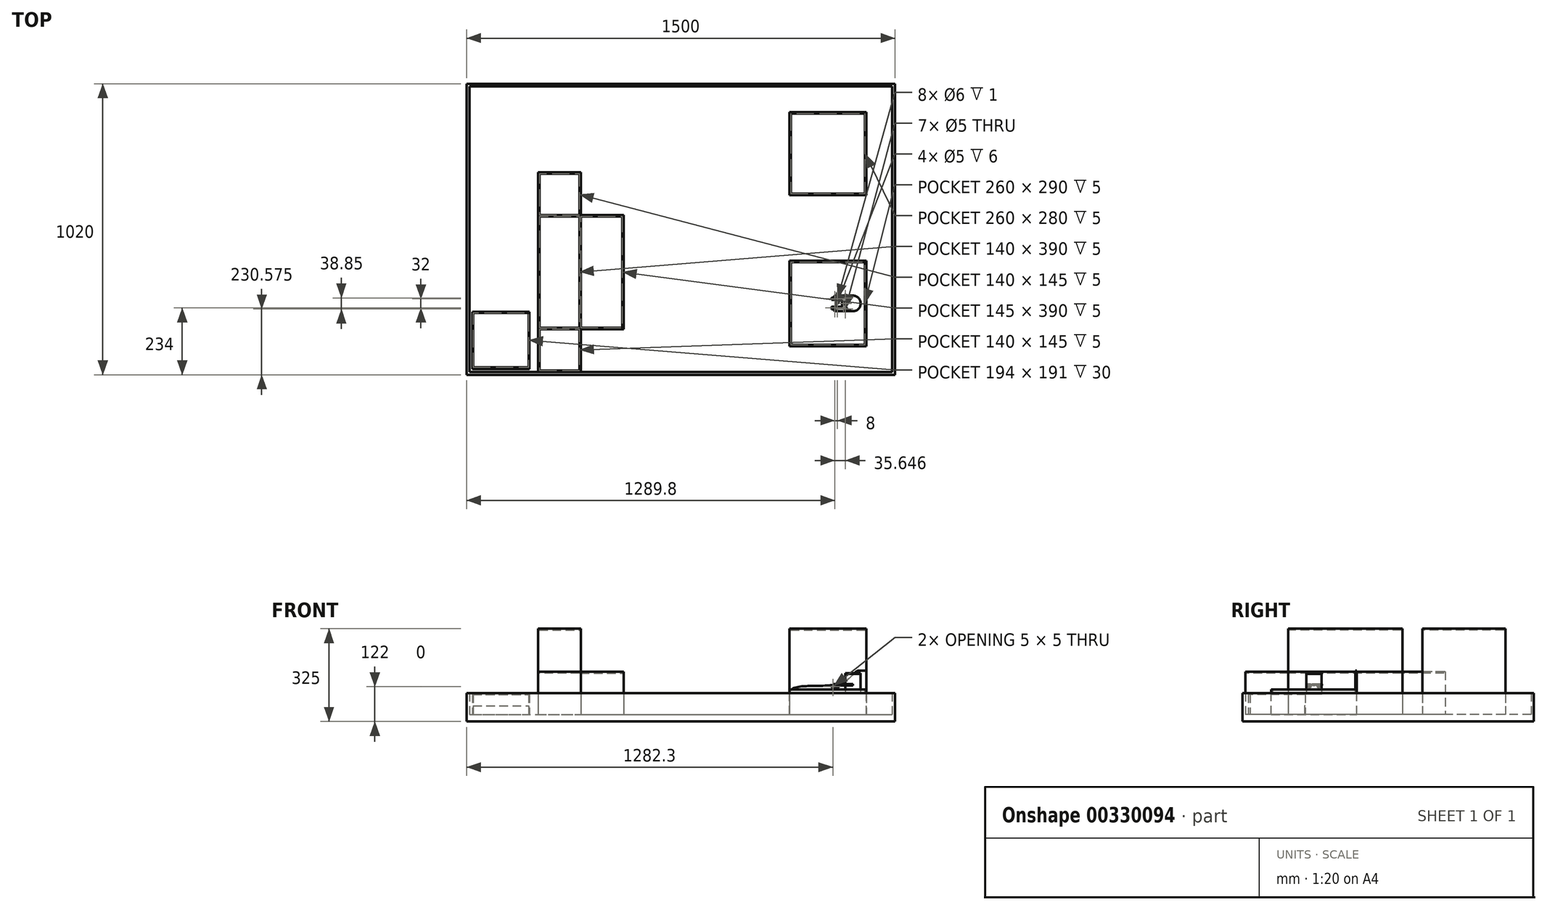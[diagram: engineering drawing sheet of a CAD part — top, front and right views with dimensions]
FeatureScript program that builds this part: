
annotation { "Feature Type Name" : "Feature", "Feature Type Description" : "" }
export const myFeature = defineFeature(function(context is Context, id is Id, definition is map)
    precondition{}
    {
        {
            var Q0;
            Q0=qCreatedBy(makeId("Top.planeOp"),FACE);
            var sketch = newSketch(context, id + "F0", { "sketchPlane" : qUnion([Q0])});
            skCircle(sketch, "E0", {"center": v(0, 0) * mm, "radius": 27.2 * mm});
            skSolve(sketch);
        }
        {
            var Q0;
            Q0=qSketchRegion(id+"F0",true);
            extrude(context, id + "F1", {"entities" : qUnion([Q0]), "depth" : 2.83 * mm});
        }
        {
            var Q0;
            Q0=makeQuery(id+"F1.opExtrude","CAP_FACE",FACE,{"disambiguationData":[OSD([sQuery(id+"F0.wireOp",EDGE,"E0")])],"isStart":false});
            var sketch = newSketch(context, id + "F2", { "sketchPlane" : qUnion([Q0])});
            skCircle(sketch, "E1", {"center": v(0, 0) * mm, "radius": 26.4 * mm});
            skSolve(sketch);
        }
        {
            var Q0;
            Q0=qSketchRegion(id+"F2",true);
            extrude(context, id + "F3", {"entities" : qUnion([Q0]), "operationType" : NewBodyOperationType.ADD, "depth" : 67.36 * mm});
        }
        {
            var Q0;
            Q0=makeQuery(id+"F3.opExtrude","CAP_FACE",FACE,{"disambiguationData":[OSD([sQuery(id+"F2.wireOp",EDGE,"E1")])],"isStart":false});
            var sketch = newSketch(context, id + "F4", { "sketchPlane" : qUnion([Q0])});
            skCircle(sketch, "E2", {"center": v(0, 0) * mm, "radius": 27.2 * mm});
            skSolve(sketch);
        }
        {
            var Q0;
            Q0=qSketchRegion(id+"F4",true);
            extrude(context, id + "F5", {"entities" : qUnion([Q0]), "operationType" : NewBodyOperationType.ADD, "depth" : 2.83 * mm});
        }
        {
            var Q0;
            Q0=makeQuery(id+"F5.opExtrude","CAP_FACE",FACE,{"disambiguationData":[OSD([sQuery(id+"F4.wireOp",EDGE,"E2")])],"isStart":false});
            var sketch = newSketch(context, id + "F6", { "sketchPlane" : qUnion([Q0])});
            skSolve(sketch);
        }
        {
            var Q0;
            Q0=qCreatedBy(makeId("Top.planeOp"),FACE);
            cPlane(context, id + "F7", {"entities" : qUnion([Q0]), "cplaneType" : CPlaneType.OFFSET, "offset" : 25 * mm, "width" : 150 * mm, "height" : 150 * mm});
        }
        {
            var Q0;
            Q0=makeQuery(id+"F6.imprint","IMPRINT",FACE,{"disambiguationData":[TD([[makeQuery(id+"F6.imprint","IMPRINT",EDGE,{"derivedFrom":makeQuery(id+"F5.opExtrude","CAP_EDGE",EDGE,{"disambiguationData":[OSD([sQuery(id+"F4.wireOp",EDGE,"E2")])],"isStart":false})}),1.0]])]});
            var sketch = newSketch(context, id + "F8", { "sketchPlane" : qUnion([Q0])});
            skSolve(sketch);
        }
        {
            var Q0;
            Q0=qCreatedBy(makeId("Top.planeOp"),FACE);
            var sketch = newSketch(context, id + "F9", { "sketchPlane" : qUnion([Q0])});
            skLineSegment(sketch, "E3.bottom", {"start": v(-222.8, -150) * mm, "end": v(47.2, -150) * mm});
            skLineSegment(sketch, "E3.top", {"start": v(-222.8, 150) * mm, "end": v(47.2, 150) * mm});
            skLineSegment(sketch, "E3.left", {"start": v(-222.8, -150) * mm, "end": v(-222.8, 150) * mm});
            skLineSegment(sketch, "E3.right", {"start": v(47.2, -150) * mm, "end": v(47.2, 150) * mm});
            skSolve(sketch);
        }
        {
            var Q0;
            Q0=qSketchRegion(id+"F9",true);
            extrude(context, id + "F10", {"entities" : qUnion([Q0]), "oppositeDirection" : true, "depth" : 72 * mm});
        }
        {
            var Q0;
            Q0=makeQuery(id+"F10.opExtrude","CAP_FACE",FACE,{"disambiguationData":[OSD([sQuery(id+"F9.wireOp",EDGE,"E3.bottom"),sQuery(id+"F9.wireOp",EDGE,"E3.top"),sQuery(id+"F9.wireOp",EDGE,"E3.left"),sQuery(id+"F9.wireOp",EDGE,"E3.right")])],"isStart":true});
            var sketch = newSketch(context, id + "F11", { "sketchPlane" : qUnion([Q0])});
            skLineSegment(sketch, "E4.bottom", {"start": v(-222.8, -150) * mm, "end": v(47.2, -150) * mm});
            skLineSegment(sketch, "E4.top", {"start": v(-222.8, -145) * mm, "end": v(42.2, -145) * mm});
            skLineSegment(sketch, "E4.left", {"start": v(-222.8, -150) * mm, "end": v(-222.8, -145) * mm});
            skLineSegment(sketch, "E5.bottom", {"start": v(47.2, 150) * mm, "end": v(42.2, 150) * mm});
            skLineSegment(sketch, "E5.left", {"start": v(47.2, 150) * mm, "end": v(47.2, -150) * mm});
            skLineSegment(sketch, "E5.right", {"start": v(42.2, 150) * mm, "end": v(42.2, -145) * mm});
            skSolve(sketch);
        }
        {
            var Q0;
            Q0=qSketchRegion(id+"F11",true);
            extrude(context, id + "F12", {"entities" : qUnion([Q0]), "operationType" : NewBodyOperationType.ADD, "depth" : 15 * mm});
        }
        {
            var Q0;
            Q0=makeQuery(id+"F12.boolean.opBoolean","MERGE",FACE,{"derivedFrom":[makeQuery(id+"F10.opExtrude","SWEPT_FACE",FACE,{"disambiguationData":[OSD([sQuery(id+"F9.wireOp",EDGE,"E3.top")])]}),makeQuery(id+"F12.opExtrude","SWEPT_FACE",FACE,{"disambiguationData":[OSD([sQuery(id+"F11.wireOp",EDGE,"E5.bottom")])]})]});
            var sketch = newSketch(context, id + "F13", { "sketchPlane" : qUnion([Q0])});
            skLineSegment(sketch, "E6", {"start": v(-47.2, 81.36) * mm, "end": v(-21.31, 81.36) * mm});
            skFitSpline(sketch, "E7", {"points": [v(-21.31, 81.36) * mm, v(15.24, 52.01) * mm, v(114.14, 28.17) * mm, v(222.8, 0) * mm], "startDerivative": vector(181.02, 0.3) * mm, "endDerivative": vector(-1.73, -239.85) * mm});
            skLineSegment(sketch, "E8", {"start": v(-47.2, 81.36) * mm, "end": v(-47.2, -72) * mm});
            skLineSegment(sketch, "E9", {"start": v(-47.2, -72) * mm, "end": v(222.8, -72) * mm});
            skLineSegment(sketch, "E10", {"start": v(222.8, -72) * mm, "end": v(222.8, 0) * mm});
            skSolve(sketch);
        }
        {
            var Q0;
            Q0=qSketchRegion(id+"F13",true);
            extrude(context, id + "F14", {"entities" : qUnion([Q0]), "operationType" : NewBodyOperationType.ADD, "oppositeDirection" : true, "depth" : 5 * mm});
        }
        {
            var Q0;
            Q0=makeQuery(id+"F10.opExtrude","CAP_FACE",FACE,{"disambiguationData":[OSD([sQuery(id+"F9.wireOp",EDGE,"E3.bottom"),sQuery(id+"F9.wireOp",EDGE,"E3.top"),sQuery(id+"F9.wireOp",EDGE,"E3.left"),sQuery(id+"F9.wireOp",EDGE,"E3.right")])],"isStart":true});
            var sketch = newSketch(context, id + "F15", { "sketchPlane" : qUnion([Q0])});
            skLineSegment(sketch, "E11.bottom", {"start": v(-222.8, 145) * mm, "end": v(-217.8, 145) * mm});
            skLineSegment(sketch, "E11.top", {"start": v(-222.8, -145) * mm, "end": v(-217.8, -145) * mm});
            skLineSegment(sketch, "E11.left", {"start": v(-222.8, 145) * mm, "end": v(-222.8, -145) * mm});
            skLineSegment(sketch, "E11.right", {"start": v(-217.8, 145) * mm, "end": v(-217.8, -145) * mm});
            skSolve(sketch);
        }
        {
            var Q0;
            Q0=qSketchRegion(id+"F15",true);
            extrude(context, id + "F16", {"entities" : qUnion([Q0]), "operationType" : NewBodyOperationType.ADD, "depth" : 5 * mm});
        }
        {
            var Q0;
            Q0=makeQuery(id+"F10.opExtrude","CAP_FACE",FACE,{"disambiguationData":[OSD([sQuery(id+"F9.wireOp",EDGE,"E3.bottom"),sQuery(id+"F9.wireOp",EDGE,"E3.top"),sQuery(id+"F9.wireOp",EDGE,"E3.left"),sQuery(id+"F9.wireOp",EDGE,"E3.right")])],"isStart":false});
            var sketch = newSketch(context, id + "F17", { "sketchPlane" : qUnion([Q0])});
            skLineSegment(sketch, "E12.bottom", {"start": v(147.2, 250) * mm, "end": v(-1352.8, 250) * mm});
            skLineSegment(sketch, "E12.top", {"start": v(147.2, -770) * mm, "end": v(-1352.8, -770) * mm});
            skLineSegment(sketch, "E12.left", {"start": v(147.2, 250) * mm, "end": v(147.2, -770) * mm});
            skLineSegment(sketch, "E12.right", {"start": v(-1352.8, 250) * mm, "end": v(-1352.8, -770) * mm});
            skSolve(sketch);
        }
        {
            var Q0;
            Q0=qSketchRegion(id+"F17",true);
            extrude(context, id + "F18", {"entities" : qUnion([Q0]), "operationType" : NewBodyOperationType.ADD, "depth" : 25 * mm});
        }
        {
            var Q0;
            Q0=makeQuery(id+"F18.opExtrude","CAP_FACE",FACE,{"disambiguationData":[OSD([sQuery(id+"F17.wireOp",EDGE,"E12.bottom"),sQuery(id+"F17.wireOp",EDGE,"E12.top"),sQuery(id+"F17.wireOp",EDGE,"E12.left"),sQuery(id+"F17.wireOp",EDGE,"E12.right")])],"isStart":true});
            var sketch = newSketch(context, id + "F19", { "sketchPlane" : qUnion([Q0])});
            skLineSegment(sketch, "E13.bottom", {"start": v(-222.8, 670) * mm, "end": v(47.2, 670) * mm});
            skLineSegment(sketch, "E13.top", {"start": v(-222.8, 380) * mm, "end": v(47.2, 380) * mm});
            skLineSegment(sketch, "E13.left", {"start": v(-222.8, 670) * mm, "end": v(-222.8, 380) * mm});
            skLineSegment(sketch, "E13.right", {"start": v(47.2, 670) * mm, "end": v(47.2, 380) * mm});
            skSolve(sketch);
        }
        {
            var Q0;
            Q0=qSketchRegion(id+"F19",true);
            extrude(context, id + "F20", {"entities" : qUnion([Q0]), "operationType" : NewBodyOperationType.ADD, "depth" : 300 * mm});
        }
        {
            var Q0;
            Q0=makeQuery(id+"F20.opExtrude","CAP_FACE",FACE,{"disambiguationData":[OSD([sQuery(id+"F19.wireOp",EDGE,"E13.bottom"),sQuery(id+"F19.wireOp",EDGE,"E13.top"),sQuery(id+"F19.wireOp",EDGE,"E13.left"),sQuery(id+"F19.wireOp",EDGE,"E13.right")])],"isStart":false});
            var sketch = newSketch(context, id + "F21", { "sketchPlane" : qUnion([Q0])});
            skLineSegment(sketch, "E14.bottom", {"start": v(-217.8, 665) * mm, "end": v(42.2, 665) * mm});
            skLineSegment(sketch, "E14.top", {"start": v(-217.8, 385) * mm, "end": v(42.2, 385) * mm});
            skLineSegment(sketch, "E14.left", {"start": v(-217.8, 665) * mm, "end": v(-217.8, 385) * mm});
            skLineSegment(sketch, "E14.right", {"start": v(42.2, 665) * mm, "end": v(42.2, 385) * mm});
            skSolve(sketch);
        }
        {
            var Q0;
            Q0=qSketchRegion(id+"F21",true);
            extrude(context, id + "F22", {"entities" : qUnion([Q0]), "operationType" : NewBodyOperationType.REMOVE, "oppositeDirection" : true, "depth" : 5 * mm});
        }
        {
            var Q0;
            Q0=makeQuery(id+"F18.opExtrude","CAP_FACE",FACE,{"disambiguationData":[OSD([sQuery(id+"F17.wireOp",EDGE,"E12.bottom"),sQuery(id+"F17.wireOp",EDGE,"E12.top"),sQuery(id+"F17.wireOp",EDGE,"E12.left"),sQuery(id+"F17.wireOp",EDGE,"E12.right")])],"isStart":true});
            var sketch = newSketch(context, id + "F23", { "sketchPlane" : qUnion([Q0])});
            skLineSegment(sketch, "E15.bottom", {"start": v(-1352.8, 770) * mm, "end": v(147.2, 770) * mm});
            skLineSegment(sketch, "E15.top", {"start": v(-1352.8, -250) * mm, "end": v(147.2, -250) * mm});
            skLineSegment(sketch, "E15.left", {"start": v(-1352.8, 770) * mm, "end": v(-1352.8, -250) * mm});
            skLineSegment(sketch, "E15.right", {"start": v(147.2, 770) * mm, "end": v(147.2, -250) * mm});
            skLineSegment(sketch, "E16.bottom", {"start": v(-1342.8, 760) * mm, "end": v(137.2, 760) * mm});
            skLineSegment(sketch, "E16.top", {"start": v(-1342.8, -240) * mm, "end": v(137.2, -240) * mm});
            skLineSegment(sketch, "E16.left", {"start": v(-1342.8, 760) * mm, "end": v(-1342.8, -240) * mm});
            skLineSegment(sketch, "E16.right", {"start": v(137.2, 760) * mm, "end": v(137.2, -240) * mm});
            skSolve(sketch);
        }
        {
            var Q0;
            Q0=qSketchRegion(id+"F23",true);
            extrude(context, id + "F24", {"entities" : qUnion([Q0]), "operationType" : NewBodyOperationType.ADD, "depth" : 75 * mm});
        }
        {
            var Q0;
            Q0=makeQuery(id+"F18.opExtrude","CAP_FACE",FACE,{"disambiguationData":[OSD([sQuery(id+"F17.wireOp",EDGE,"E12.bottom"),sQuery(id+"F17.wireOp",EDGE,"E12.top"),sQuery(id+"F17.wireOp",EDGE,"E12.left"),sQuery(id+"F17.wireOp",EDGE,"E12.right")])],"isStart":true});
            var sketch = newSketch(context, id + "F25", { "sketchPlane" : qUnion([Q0])});
            skLineSegment(sketch, "E17.bottom", {"start": v(-1102.8, 460) * mm, "end": v(-952.8, 460) * mm});
            skLineSegment(sketch, "E17.top", {"start": v(-1102.8, -240) * mm, "end": v(-952.8, -240) * mm});
            skLineSegment(sketch, "E17.left", {"start": v(-1102.8, 460) * mm, "end": v(-1102.8, -240) * mm});
            skLineSegment(sketch, "E17.right", {"start": v(-952.8, 460) * mm, "end": v(-952.8, 310) * mm});
            skLineSegment(sketch, "E18.bottom", {"start": v(-952.8, 310) * mm, "end": v(-802.8, 310) * mm});
            skLineSegment(sketch, "E18.top", {"start": v(-952.8, -90) * mm, "end": v(-802.8, -90) * mm});
            skLineSegment(sketch, "E18.right", {"start": v(-802.8, 310) * mm, "end": v(-802.8, -90) * mm});
            skLineSegment(sketch, "E19.trimOffspring", {"start": v(-952.8, -90) * mm, "end": v(-952.8, -240) * mm});
            skSolve(sketch);
        }
        {
            var Q0;
            Q0=qSketchRegion(id+"F25",true);
            extrude(context, id + "F26", {"entities" : qUnion([Q0]), "operationType" : NewBodyOperationType.ADD, "depth" : 150 * mm});
        }
        {
            var Q0;
            Q0=makeQuery(id+"F26.opExtrude","CAP_FACE",FACE,{"disambiguationData":[OSD([sQuery(id+"F25.wireOp",EDGE,"E17.bottom"),sQuery(id+"F25.wireOp",EDGE,"E17.top"),sQuery(id+"F25.wireOp",EDGE,"E17.left"),sQuery(id+"F25.wireOp",EDGE,"E17.right"),sQuery(id+"F25.wireOp",EDGE,"E18.bottom"),sQuery(id+"F25.wireOp",EDGE,"E18.top"),sQuery(id+"F25.wireOp",EDGE,"E18.right"),sQuery(id+"F25.wireOp",EDGE,"E19.trimOffspring")])],"isStart":false});
            var sketch = newSketch(context, id + "F27", { "sketchPlane" : qUnion([Q0])});
            skLineSegment(sketch, "E20.bottom", {"start": v(-952.8, 310) * mm, "end": v(-1102.8, 310) * mm});
            skLineSegment(sketch, "E20.top", {"start": v(-952.8, -90) * mm, "end": v(-1102.8, -90) * mm});
            skLineSegment(sketch, "E20.left", {"start": v(-952.8, 310) * mm, "end": v(-952.8, -90) * mm});
            skLineSegment(sketch, "E20.right", {"start": v(-1102.8, 310) * mm, "end": v(-1102.8, -90) * mm});
            skSolve(sketch);
        }
        {
            var Q0;
            Q0=qSketchRegion(id+"F27",true);
            extrude(context, id + "F28", {"entities" : qUnion([Q0]), "operationType" : NewBodyOperationType.ADD, "depth" : 150 * mm});
        }
        {
            var Q0;
            Q0=makeQuery(id+"F28.opExtrude","CAP_FACE",FACE,{"disambiguationData":[OSD([sQuery(id+"F27.wireOp",EDGE,"E20.bottom"),sQuery(id+"F27.wireOp",EDGE,"E20.top"),sQuery(id+"F27.wireOp",EDGE,"E20.left"),sQuery(id+"F27.wireOp",EDGE,"E20.right")])],"isStart":false});
            var sketch = newSketch(context, id + "F29", { "sketchPlane" : qUnion([Q0])});
            skLineSegment(sketch, "E21.bottom", {"start": v(-1097.8, 305) * mm, "end": v(-957.8, 305) * mm});
            skLineSegment(sketch, "E21.top", {"start": v(-1097.8, -85) * mm, "end": v(-957.8, -85) * mm});
            skLineSegment(sketch, "E21.left", {"start": v(-1097.8, 305) * mm, "end": v(-1097.8, -85) * mm});
            skLineSegment(sketch, "E21.right", {"start": v(-957.8, 305) * mm, "end": v(-957.8, -85) * mm});
            skSolve(sketch);
        }
        {
            var Q0;
            Q0=qSketchRegion(id+"F29",true);
            extrude(context, id + "F30", {"entities" : qUnion([Q0]), "operationType" : NewBodyOperationType.REMOVE, "oppositeDirection" : true, "depth" : 5 * mm});
        }
        {
            var Q0;
            {var subQ0=sQuery(id+"F25.wireOp",EDGE,"E17.left");var subQ1=sQuery(id+"F25.wireOp",EDGE,"E18.bottom");var subQ2=sQuery(id+"F25.wireOp",EDGE,"E17.right");var subQ3=sQuery(id+"F25.wireOp",EDGE,"E17.bottom");var subQ4=makeQuery(id+"F26.opExtrude","CAP_FACE",FACE,{"disambiguationData":[OSD([subQ3,sQuery(id+"F25.wireOp",EDGE,"E17.top"),subQ0,subQ2,subQ1,sQuery(id+"F25.wireOp",EDGE,"E18.top"),sQuery(id+"F25.wireOp",EDGE,"E18.right"),sQuery(id+"F25.wireOp",EDGE,"E19.trimOffspring")])],"isStart":false});Q0=makeQuery(id+"F28.boolean.opBoolean","SPLIT",FACE,{"disambiguationData":[TD([makeQuery(id+"F26.opExtrude","SWEPT_FACE",FACE,{"disambiguationData":[OSD([subQ3])]})])],"derivedFrom":subQ4});}
            var sketch = newSketch(context, id + "F31", { "sketchPlane" : qUnion([Q0])});
            skLineSegment(sketch, "E22.bottom", {"start": v(-1097.8, 455) * mm, "end": v(-957.8, 455) * mm});
            skLineSegment(sketch, "E22.top", {"start": v(-1097.8, 310) * mm, "end": v(-957.8, 310) * mm});
            skLineSegment(sketch, "E22.left", {"start": v(-1097.8, 455) * mm, "end": v(-1097.8, 310) * mm});
            skLineSegment(sketch, "E22.right", {"start": v(-957.8, 455) * mm, "end": v(-957.8, 310) * mm});
            skLineSegment(sketch, "E23.bottom", {"start": v(-952.8, 305) * mm, "end": v(-807.8, 305) * mm});
            skLineSegment(sketch, "E23.top", {"start": v(-952.8, -85) * mm, "end": v(-807.8, -85) * mm});
            skLineSegment(sketch, "E23.left", {"start": v(-952.8, 305) * mm, "end": v(-952.8, -85) * mm});
            skLineSegment(sketch, "E23.right", {"start": v(-807.8, 305) * mm, "end": v(-807.8, -85) * mm});
            skLineSegment(sketch, "E24.bottom", {"start": v(-1097.8, -90) * mm, "end": v(-957.8, -90) * mm});
            skLineSegment(sketch, "E24.top", {"start": v(-1097.8, -235) * mm, "end": v(-957.8, -235) * mm});
            skLineSegment(sketch, "E24.left", {"start": v(-1097.8, -90) * mm, "end": v(-1097.8, -235) * mm});
            skLineSegment(sketch, "E24.right", {"start": v(-957.8, -90) * mm, "end": v(-957.8, -235) * mm});
            skSolve(sketch);
        }
        {
            var Q0;
            Q0=qSketchRegion(id+"F31",true);
            extrude(context, id + "F32", {"entities" : qUnion([Q0]), "operationType" : NewBodyOperationType.REMOVE, "oppositeDirection" : true, "depth" : 5 * mm});
        }
        {
            var Q0;
            Q0=qCreatedBy(id+"F7.planeOp",FACE);
            var sketch = newSketch(context, id + "F33", { "sketchPlane" : qUnion([Q0])});
            skLineSegment(sketch, "E25", {"start": v(0, 0) * mm, "end": v(-90, 0) * mm, "construction": true});
            skLineSegment(sketch, "E26.bottom", {"start": v(-74.5, -12) * mm, "end": v(-55, -12) * mm});
            skLineSegment(sketch, "E26.top", {"start": v(-74.5, -20) * mm, "end": v(-55, -20) * mm});
            skLineSegment(sketch, "E26.left", {"start": v(-74.5, -12) * mm, "end": v(-74.5, -13) * mm});
            skPoint(sketch, "E27.visualSharp", {"position": v(-51, -12) * mm});
            skPoint(sketch, "E28.visualSharp", {"position": v(-51, -20) * mm});
            skCircle(sketch, "E29", {"center": v(-55, -16) * mm, "radius": 3 * mm});
            skLineSegment(sketch, "E30", {"start": v(-59, -3.98) * mm, "end": v(-59, -18.08) * mm, "construction": true});
            skCircle(sketch, "E31.MirrorC", {"center": v(-63, -16) * mm, "radius": 3 * mm});
            skLineSegment(sketch, "E32.bottom", {"start": v(-74.5, -13) * mm, "end": v(-65.65, -13) * mm});
            skLineSegment(sketch, "E32.top", {"start": v(-74.5, -19) * mm, "end": v(-65.65, -19) * mm});
            skArc(sketch, "E33", {"start": v(-65.65, -13) * mm, "mid": v(-67, -16) * mm, "end": v(-65.65, -19) * mm});
            skLineSegment(sketch, "E34.trimOffspring", {"start": v(-74.5, -19) * mm, "end": v(-74.5, -20) * mm});
            skArc(sketch, "E35.trimOffspring", {"start": v(-55, -20) * mm, "mid": v(-51, -16) * mm, "end": v(-55, -12) * mm});
            skLineSegment(sketch, "E36.MirrorCS", {"start": v(-74.5, 12) * mm, "end": v(-74.5, 13) * mm});
            skLineSegment(sketch, "E37.MirrorCS", {"start": v(-74.5, 19) * mm, "end": v(-74.5, 20) * mm});
            skPoint(sketch, "E38.MirrorP", {"position": v(-51, 12) * mm});
            skLineSegment(sketch, "E39.MirrorCS", {"start": v(-74.5, 12) * mm, "end": v(-55, 12) * mm});
            skPoint(sketch, "E40.MirrorP", {"position": v(-51, 20) * mm});
            skArc(sketch, "E41.MirrorCS", {"start": v(-65.65, 13) * mm, "mid": v(-67, 16) * mm, "end": v(-65.65, 19) * mm});
            skArc(sketch, "E42.MirrorCS", {"start": v(-55, 20) * mm, "mid": v(-51, 16) * mm, "end": v(-55, 12) * mm});
            skLineSegment(sketch, "E43.MirrorCS", {"start": v(-74.5, 20) * mm, "end": v(-55, 20) * mm});
            skCircle(sketch, "E44.MirrorC", {"center": v(-55, 16) * mm, "radius": 3 * mm});
            skCircle(sketch, "E45.MirrorC", {"center": v(-63, 16) * mm, "radius": 3 * mm});
            skLineSegment(sketch, "E46.MirrorCS", {"start": v(-74.5, 19) * mm, "end": v(-65.65, 19) * mm});
            skLineSegment(sketch, "E47.MirrorCS", {"start": v(-74.5, 13) * mm, "end": v(-65.65, 13) * mm});
            skSolve(sketch);
        }
        {
            var Q0;
            Q0=qSketchRegion(id+"F33",true);
            var Q1;
            Q1=qSketchRegion(id+"F36",true);
            extrude(context, id + "F34", {"entities" : qUnion([Q0, Q1]), "endBound" : BoundingType.SYMMETRIC, "depth" : 8 * mm});
        }
        {
            var Q0;
            Q0=makeQuery(id+"F34.opExtrude","CAP_EDGE",EDGE,{"disambiguationData":[OSD([sQuery(id+"F33.wireOp",EDGE,"E34.trimOffspring")])],"isStart":false});
            var Q1;
            Q1=makeQuery(id+"F34.opExtrude","CAP_EDGE",EDGE,{"disambiguationData":[OSD([sQuery(id+"F33.wireOp",EDGE,"E26.left")])],"isStart":false});
            var Q2;
            Q2=makeQuery(id+"F34.opExtrude","CAP_EDGE",EDGE,{"disambiguationData":[OSD([sQuery(id+"F33.wireOp",EDGE,"E34.trimOffspring")])],"isStart":true});
            var Q3;
            Q3=makeQuery(id+"F34.opExtrude","CAP_EDGE",EDGE,{"disambiguationData":[OSD([sQuery(id+"F33.wireOp",EDGE,"E26.left")])],"isStart":true});
            var Q4;
            Q4=makeQuery(id+"F34.opExtrude","CAP_EDGE",EDGE,{"disambiguationData":[OSD([sQuery(id+"F33.wireOp",EDGE,"E36.MirrorCS")])],"isStart":false});
            var Q5;
            Q5=makeQuery(id+"F34.opExtrude","CAP_EDGE",EDGE,{"disambiguationData":[OSD([sQuery(id+"F33.wireOp",EDGE,"E37.MirrorCS")])],"isStart":false});
            var Q6;
            Q6=makeQuery(id+"F34.opExtrude","CAP_EDGE",EDGE,{"disambiguationData":[OSD([sQuery(id+"F33.wireOp",EDGE,"E37.MirrorCS")])],"isStart":true});
            var Q7;
            Q7=makeQuery(id+"F34.opExtrude","CAP_EDGE",EDGE,{"disambiguationData":[OSD([sQuery(id+"F33.wireOp",EDGE,"E36.MirrorCS")])],"isStart":true});
            fillet(context, id + "F35", {"entities" : qUnion([Q0, Q1, Q2, Q3, Q4, Q5, Q6, Q7]), "radius" : 4 * mm, "tangentPropagation" : true, "allowEdgeOverflow" : false});
        }
        {
            var Q0;
            Q0=makeQuery(id+"F34.opExtrude","SWEPT_FACE",FACE,{"disambiguationData":[OSD([sQuery(id+"F33.wireOp",EDGE,"E26.top")])]});
            var sketch = newSketch(context, id + "F36", { "sketchPlane" : qUnion([Q0])});
            skCircle(sketch, "E48", {"center": v(-70.5, 25) * mm, "radius": 3 * mm});
            skSolve(sketch);
        }
        {
            var Q0;
            Q0=qSketchRegion(id+"F36",true);
            var Q1;
            Q1=makeQuery(id+"F34.opExtrude","SWEPT_FACE",FACE,{"disambiguationData":[OSD([sQuery(id+"F33.wireOp",EDGE,"E26.bottom")])]});
            extrude(context, id + "F37", {"entities" : qUnion([Q0]), "operationType" : NewBodyOperationType.ADD, "endBound" : BoundingType.UP_TO_SURFACE, "oppositeDirection" : true, "endBoundEntityFace" : qUnion([Q1]), "depth" : 25 * mm});
        }
        {
            var Q0;
            Q0=makeQuery(id+"F34.opExtrude","SWEPT_FACE",FACE,{"disambiguationData":[OSD([sQuery(id+"F33.wireOp",EDGE,"E43.MirrorCS")])]});
            var sketch = newSketch(context, id + "F38", { "sketchPlane" : qUnion([Q0])});
            skCircle(sketch, "E49", {"center": v(70.5, 25) * mm, "radius": 3 * mm});
            skSolve(sketch);
        }
        {
            var Q0;
            Q0=qSketchRegion(id+"F38",true);
            var Q1;
            Q1=makeQuery(id+"F34.opExtrude","SWEPT_FACE",FACE,{"disambiguationData":[OSD([sQuery(id+"F33.wireOp",EDGE,"E39.MirrorCS")])]});
            extrude(context, id + "F39", {"entities" : qUnion([Q0]), "operationType" : NewBodyOperationType.ADD, "endBound" : BoundingType.UP_TO_SURFACE, "oppositeDirection" : true, "endBoundEntityFace" : qUnion([Q1]), "depth" : 25 * mm});
        }
        {
            var Q0;
            Q0=qCreatedBy(id+"F7.planeOp",FACE);
            var sketch = newSketch(context, id + "F40", { "sketchPlane" : qUnion([Q0])});
            skCircle(sketch, "E50", {"center": v(-55, 16) * mm, "radius": 3 * mm});
            skCircle(sketch, "E51", {"center": v(-63, 16) * mm, "radius": 2.5 * mm});
            skCircle(sketch, "E52", {"center": v(-63, 16) * mm, "radius": 3 * mm});
            skCircle(sketch, "E53", {"center": v(-55, 16) * mm, "radius": 2.5 * mm});
            skSolve(sketch);
        }
        {
            var Q0;
            Q0=qSketchRegion(id+"F40",true);
            extrude(context, id + "F41", {"entities" : qUnion([Q0]), "operationType" : NewBodyOperationType.ADD, "endBound" : BoundingType.SYMMETRIC, "depth" : 6 * mm});
        }
        {
            var Q0;
            Q0=qCreatedBy(id+"F7.planeOp",FACE);
            var sketch = newSketch(context, id + "F42", { "sketchPlane" : qUnion([Q0])});
            skCircle(sketch, "E54", {"center": v(-63, -16) * mm, "radius": 2.5 * mm});
            skCircle(sketch, "E55", {"center": v(-63, -16) * mm, "radius": 3 * mm});
            skCircle(sketch, "E56", {"center": v(-55, -16) * mm, "radius": 2.5 * mm});
            skCircle(sketch, "E57", {"center": v(-55, -16) * mm, "radius": 3 * mm});
            skSolve(sketch);
        }
        {
            var Q0;
            Q0=qSketchRegion(id+"F42",true);
            extrude(context, id + "F43", {"entities" : qUnion([Q0]), "operationType" : NewBodyOperationType.ADD, "endBound" : BoundingType.SYMMETRIC, "depth" : 6 * mm});
        }
        {
            var Q0;
            Q0=makeQuery(id+"F34.opExtrude","SWEPT_FACE",FACE,{"disambiguationData":[OSD([sQuery(id+"F33.wireOp",EDGE,"E43.MirrorCS")])]});
            var sketch = newSketch(context, id + "F44", { "sketchPlane" : qUnion([Q0])});
            skArc(sketch, "E58", {"start": v(71.5, 27.3) * mm, "mid": v(70.5, 27.5) * mm, "end": v(69.5, 27.3) * mm});
            skLineSegment(sketch, "E59.bottom", {"start": v(68.2, 26) * mm, "end": v(69.5, 26) * mm});
            skLineSegment(sketch, "E59.top", {"start": v(68.2, 24) * mm, "end": v(69.5, 24) * mm});
            skLineSegment(sketch, "E60.left", {"start": v(71.5, 27.3) * mm, "end": v(71.5, 26) * mm});
            skLineSegment(sketch, "E60.right", {"start": v(69.5, 27.3) * mm, "end": v(69.5, 26) * mm});
            skPoint(sketch, "E61.orphan", {"position": v(69.5, 27.8) * mm});
            skPoint(sketch, "E62.orphan", {"position": v(71.5, 27.8) * mm});
            skArc(sketch, "E63.trimOffspring", {"start": v(68.2, 26) * mm, "mid": v(68, 25) * mm, "end": v(68.2, 24) * mm});
            skPoint(sketch, "E59.left.start.orphan", {"position": v(67.32, 26) * mm});
            skPoint(sketch, "E64.orphan", {"position": v(67.32, 24) * mm});
            skArc(sketch, "E65.trimOffspring", {"start": v(69.5, 22.7) * mm, "mid": v(70.5, 22.5) * mm, "end": v(71.5, 22.7) * mm});
            skLineSegment(sketch, "E66.trimOffspring", {"start": v(69.5, 24) * mm, "end": v(69.5, 22.7) * mm});
            skLineSegment(sketch, "E67.trimOffspring", {"start": v(71.5, 26) * mm, "end": v(72.8, 26) * mm});
            skLineSegment(sketch, "E68.trimOffspring", {"start": v(71.5, 24) * mm, "end": v(71.5, 22.7) * mm});
            skLineSegment(sketch, "E69.trimOffspring", {"start": v(71.5, 24) * mm, "end": v(72.8, 24) * mm});
            skPoint(sketch, "E60.top.end.orphan", {"position": v(69.5, 22.2) * mm});
            skPoint(sketch, "E70.orphan", {"position": v(71.5, 22.2) * mm});
            skPoint(sketch, "E59.right.end.orphan", {"position": v(73.68, 24) * mm});
            skPoint(sketch, "E71.orphan", {"position": v(73.68, 26) * mm});
            skArc(sketch, "E72.trimOffspring", {"start": v(72.8, 24) * mm, "mid": v(73, 25) * mm, "end": v(72.8, 26) * mm});
            skSolve(sketch);
        }
        {
            var Q0;
            Q0=qSketchRegion(id+"F44",true);
            extrude(context, id + "F45", {"entities" : qUnion([Q0]), "operationType" : NewBodyOperationType.REMOVE, "endBound" : BoundingType.THROUGH_ALL, "oppositeDirection" : true, "depth" : 25 * mm});
        }
        {
            var Q0;
            Q0=makeQuery(id+"F18.opExtrude","CAP_FACE",FACE,{"disambiguationData":[OSD([sQuery(id+"F17.wireOp",EDGE,"E12.bottom"),sQuery(id+"F17.wireOp",EDGE,"E12.top"),sQuery(id+"F17.wireOp",EDGE,"E12.left"),sQuery(id+"F17.wireOp",EDGE,"E12.right")])],"isStart":true});
            var sketch = newSketch(context, id + "F46", { "sketchPlane" : qUnion([Q0])});
            skLineSegment(sketch, "E73.bottom", {"start": v(-1332.8, -30) * mm, "end": v(-1132.8, -30) * mm});
            skLineSegment(sketch, "E73.top", {"start": v(-1332.8, -230) * mm, "end": v(-1132.8, -230) * mm});
            skLineSegment(sketch, "E73.left", {"start": v(-1332.8, -30) * mm, "end": v(-1332.8, -230) * mm});
            skLineSegment(sketch, "E73.right", {"start": v(-1132.8, -30) * mm, "end": v(-1132.8, -230) * mm});
            skLineSegment(sketch, "E74.bottom", {"start": v(-1329.8, -33) * mm, "end": v(-1135.8, -33) * mm});
            skLineSegment(sketch, "E74.top", {"start": v(-1329.8, -224) * mm, "end": v(-1135.8, -224) * mm});
            skLineSegment(sketch, "E74.left", {"start": v(-1329.8, -33) * mm, "end": v(-1329.8, -224) * mm});
            skLineSegment(sketch, "E74.right", {"start": v(-1135.8, -33) * mm, "end": v(-1135.8, -224) * mm});
            skSolve(sketch);
        }
        {
            var Q0;
            Q0=qSketchRegion(id+"F46",true);
            extrude(context, id + "F47", {"entities" : qUnion([Q0]), "operationType" : NewBodyOperationType.ADD, "depth" : 30 * mm});
        }
        {
            var Q0;
            Q0=makeQuery(id+"F47.opExtrude","CAP_FACE",FACE,{"disambiguationData":[OSD([sQuery(id+"F46.wireOp",EDGE,"E73.bottom"),sQuery(id+"F46.wireOp",EDGE,"E73.top"),sQuery(id+"F46.wireOp",EDGE,"E73.left"),sQuery(id+"F46.wireOp",EDGE,"E73.right"),sQuery(id+"F46.wireOp",EDGE,"E74.bottom"),sQuery(id+"F46.wireOp",EDGE,"E74.top"),sQuery(id+"F46.wireOp",EDGE,"E74.left"),sQuery(id+"F46.wireOp",EDGE,"E74.right")])],"isStart":false});
            var sketch = newSketch(context, id + "F48", { "sketchPlane" : qUnion([Q0])});
            skLineSegment(sketch, "E75.bottom", {"start": v(-1332.8, -30) * mm, "end": v(-1329.8, -30) * mm});
            skLineSegment(sketch, "E75.top", {"start": v(-1332.8, -230) * mm, "end": v(-1329.8, -230) * mm});
            skLineSegment(sketch, "E75.left", {"start": v(-1332.8, -30) * mm, "end": v(-1332.8, -230) * mm});
            skLineSegment(sketch, "E75.right", {"start": v(-1329.8, -30) * mm, "end": v(-1329.8, -224) * mm});
            skLineSegment(sketch, "E76.bottom", {"start": v(-1329.8, -230) * mm, "end": v(-1135.8, -230) * mm});
            skLineSegment(sketch, "E76.top", {"start": v(-1329.8, -224) * mm, "end": v(-1135.8, -224) * mm});
            skLineSegment(sketch, "E77.bottom", {"start": v(-1135.8, -230) * mm, "end": v(-1132.8, -230) * mm});
            skLineSegment(sketch, "E77.top", {"start": v(-1135.8, -30) * mm, "end": v(-1132.8, -30) * mm});
            skLineSegment(sketch, "E77.left", {"start": v(-1135.8, -224) * mm, "end": v(-1135.8, -30) * mm});
            skLineSegment(sketch, "E77.right", {"start": v(-1132.8, -230) * mm, "end": v(-1132.8, -30) * mm});
            skSolve(sketch);
        }
        {
            var Q0;
            Q0=qSketchRegion(id+"F48",true);
            extrude(context, id + "F49", {"entities" : qUnion([Q0]), "operationType" : NewBodyOperationType.ADD, "depth" : 40 * mm});
        }
        {
            var Q0;
            Q0=makeQuery(id+"F34.opExtrude","CAP_FACE",FACE,{"disambiguationData":[OSD([sQuery(id+"F33.wireOp",EDGE,"E26.bottom"),sQuery(id+"F33.wireOp",EDGE,"E26.top"),sQuery(id+"F33.wireOp",EDGE,"E26.left"),sQuery(id+"F33.wireOp",EDGE,"E29"),sQuery(id+"F33.wireOp",EDGE,"E31.MirrorC"),sQuery(id+"F33.wireOp",EDGE,"E32.bottom"),sQuery(id+"F33.wireOp",EDGE,"E32.top"),sQuery(id+"F33.wireOp",EDGE,"E33"),sQuery(id+"F33.wireOp",EDGE,"E34.trimOffspring"),sQuery(id+"F33.wireOp",EDGE,"E35.trimOffspring")])],"isStart":false});
            var sketch = newSketch(context, id + "F50", { "sketchPlane" : qUnion([Q0])});
            skLineSegment(sketch, "E78.bottom", {"start": v(0.39, 27.27) * mm, "end": v(-67.04, 27.27) * mm});
            skLineSegment(sketch, "E78.top", {"start": v(0.39, -27.42) * mm, "end": v(-67.04, -27.42) * mm});
            skLineSegment(sketch, "E78.left", {"start": v(0.39, 27.27) * mm, "end": v(0.39, 27.2) * mm});
            skLineSegment(sketch, "E78.right", {"start": v(-67.04, 27.27) * mm, "end": v(-67.04, 12) * mm});
            skArc(sketch, "E79.1", {"start": v(0.39, 27.2) * mm, "mid": v(-27.2, 0) * mm, "end": v(0.39, -27.2) * mm});
            skLineSegment(sketch, "E80.trimOffspring", {"start": v(0.39, -27.2) * mm, "end": v(0.39, -27.42) * mm});
            skCircle(sketch, "E81", {"center": v(-63, 16) * mm, "radius": 2.5 * mm});
            skCircle(sketch, "E82", {"center": v(-63, -16) * mm, "radius": 2.5 * mm});
            skCircle(sketch, "E83", {"center": v(-55, 16) * mm, "radius": 2.5 * mm});
            skCircle(sketch, "E84", {"center": v(-55, -16) * mm, "radius": 2.5 * mm});
            skLineSegment(sketch, "E85.bottom", {"start": v(-67.04, 12) * mm, "end": v(-37.7, 12) * mm});
            skLineSegment(sketch, "E85.top", {"start": v(-67.04, -12) * mm, "end": v(-37.7, -12) * mm});
            skLineSegment(sketch, "E85.right", {"start": v(-37.7, 12) * mm, "end": v(-37.7, -12) * mm});
            skLineSegment(sketch, "E86.trimOffspring", {"start": v(-67.04, -12) * mm, "end": v(-67.04, -27.42) * mm});
            skCircle(sketch, "E87", {"center": v(-32.8, 0) * mm, "radius": 2.5 * mm});
            skCircle(sketch, "E88", {"center": v(-27.35, 19.43) * mm, "radius": 2.5 * mm});
            skLineSegment(sketch, "E89", {"start": v(-93.02, 0) * mm, "end": v(2.52, 0) * mm, "construction": true});
            skCircle(sketch, "E90.MirrorC", {"center": v(-27.35, -19.43) * mm, "radius": 2.5 * mm});
            skSolve(sketch);
        }
        {
            var Q0;
            Q0 = qSketchRegion(id + "F50", true);
            var Q1;
            {var subQ4=sQuery(id+"F50.wireOp",EDGE,"E78.bottom");Q1=makeQuery(id+"F50.imprint","IMPRINT",FACE,{"disambiguationData":[TD([[makeQuery(id+"F50.imprint","IMPRINT",EDGE,{"derivedFrom":subQ4}),1.0]])]});}
            extrude(context, id + "F51", {"entities" : qUnion([Q0, Q1]), "depth" : 5 * mm});
        }
        {
            var Q0;
            Q0=makeQuery(id+"F51.opExtrude","SWEPT_EDGE",EDGE,{"disambiguationData":[OSD([sQuery(id+"F50.wireOp",EDGE,"E85.bottom"),sQuery(id+"F50.wireOp",EDGE,"E85.right")])]});
            var Q1;
            Q1=makeQuery(id+"F51.opExtrude","SWEPT_EDGE",EDGE,{"disambiguationData":[OSD([sQuery(id+"F50.wireOp",EDGE,"E85.top"),sQuery(id+"F50.wireOp",EDGE,"E85.right")])]});
            var Q2;
            Q2=makeQuery(id+"F51.opExtrude","SWEPT_EDGE",EDGE,{"disambiguationData":[OSD([sQuery(id+"F50.wireOp",EDGE,"E78.bottom"),sQuery(id+"F50.wireOp",EDGE,"E78.right")])]});
            var Q3;
            Q3=makeQuery(id+"F51.opExtrude","SWEPT_EDGE",EDGE,{"disambiguationData":[OSD([sQuery(id+"F50.wireOp",EDGE,"E78.right"),sQuery(id+"F50.wireOp",EDGE,"E85.bottom")])]});
            var Q4;
            Q4=makeQuery(id+"F51.opExtrude","SWEPT_EDGE",EDGE,{"disambiguationData":[OSD([sQuery(id+"F50.wireOp",EDGE,"E78.top"),sQuery(id+"F50.wireOp",EDGE,"E86.trimOffspring")])]});
            var Q5;
            Q5=makeQuery(id+"F51.opExtrude","SWEPT_EDGE",EDGE,{"disambiguationData":[OSD([sQuery(id+"F33.wireOp",EDGE,"E26.bottom"),sQuery(id+"F50.wireOp",EDGE,"E85.top"),sQuery(id+"F50.wireOp",EDGE,"E86.trimOffspring")])]});
            fillet(context, id + "F52", {"entities" : qUnion([Q0, Q1, Q2, Q3, Q4, Q5]), "radius" : 5 * mm, "tangentPropagation" : true, "allowEdgeOverflow" : false});
        }
    });
